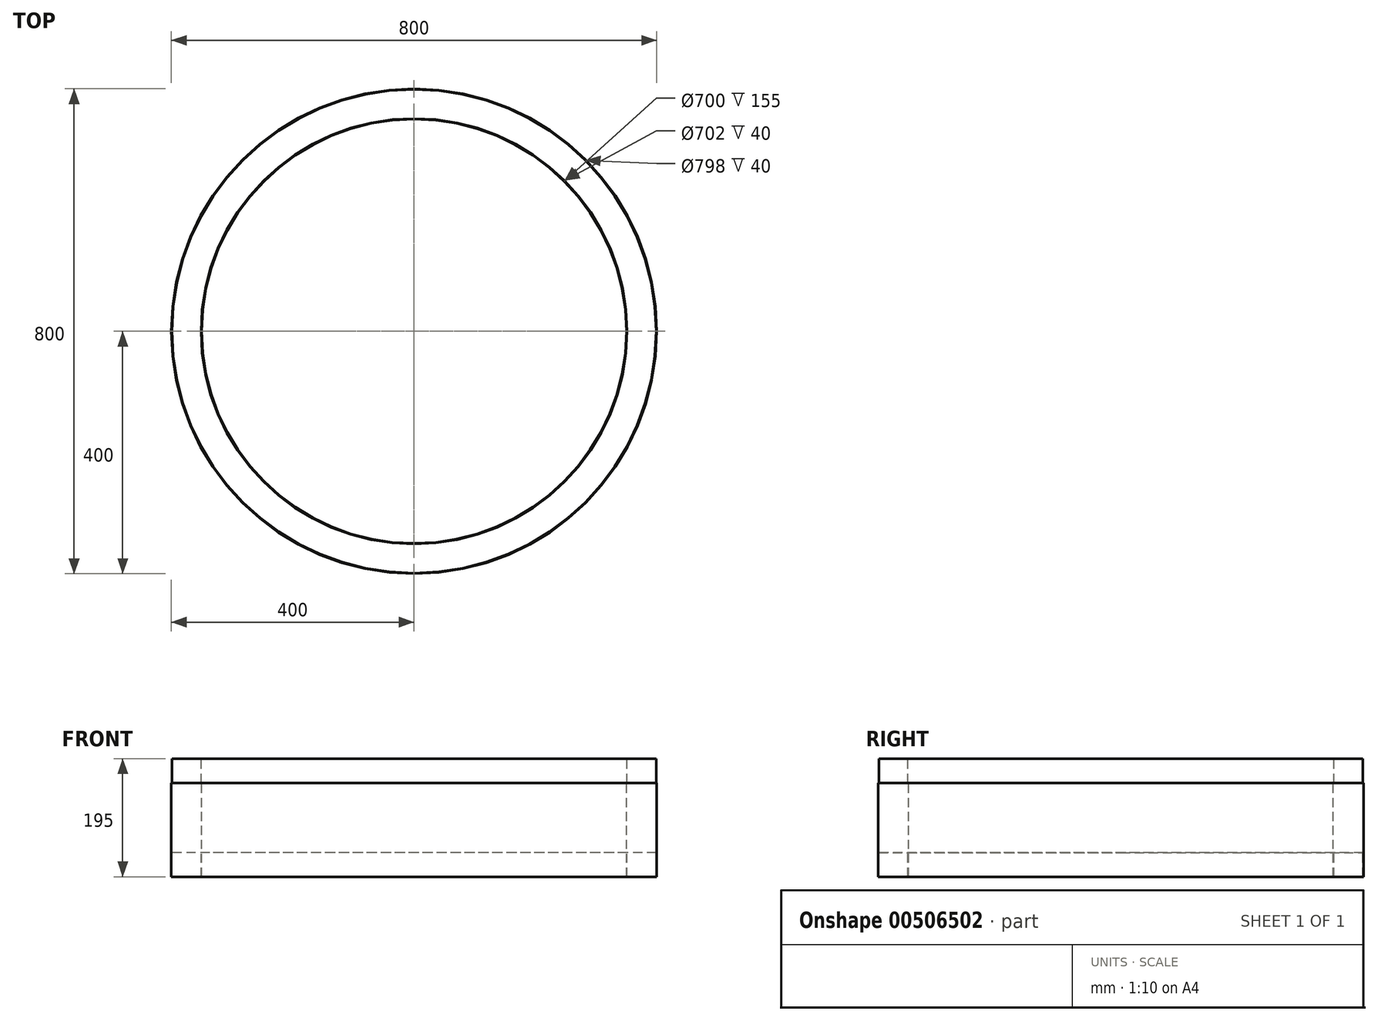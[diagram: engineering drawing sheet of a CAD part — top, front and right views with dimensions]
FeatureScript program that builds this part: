
annotation { "Feature Type Name" : "Feature", "Feature Type Description" : "" }
export const myFeature = defineFeature(function(context is Context, id is Id, definition is map)
    precondition{}
    {
        {
            var Q0;
            Q0=qCreatedBy(makeId("Front.planeOp"),FACE);
            var sketch = newSketch(context, id + "F0", { "sketchPlane" : qUnion([Q0])});
            skLineSegment(sketch, "E0", {"start": v(0, 74.87) * mm, "end": v(0, -73.71) * mm, "construction": true});
            skLineSegment(sketch, "E1", {"start": v(0, 374.84) * mm, "end": v(0, -528.94) * mm, "construction": true});
            skLineSegment(sketch, "E2", {"start": v(-350, -489.75) * mm, "end": v(-350, -334.75) * mm});
            skLineSegment(sketch, "E3", {"start": v(-350, -334.75) * mm, "end": v(-351, -334.75) * mm});
            skLineSegment(sketch, "E4", {"start": v(-351, -334.75) * mm, "end": v(-351, -294.75) * mm});
            skLineSegment(sketch, "E5", {"start": v(-351, -294.75) * mm, "end": v(-399, -294.75) * mm});
            skLineSegment(sketch, "E6", {"start": v(-399, -294.75) * mm, "end": v(-399, -334.75) * mm});
            skLineSegment(sketch, "E7", {"start": v(-399, -334.75) * mm, "end": v(-400, -334.75) * mm});
            skLineSegment(sketch, "E8", {"start": v(-400, -334.75) * mm, "end": v(-400, -489.75) * mm});
            skLineSegment(sketch, "E9", {"start": v(-400, -489.75) * mm, "end": v(-399, -489.75) * mm});
            skLineSegment(sketch, "E10", {"start": v(-399, -489.75) * mm, "end": v(-399, -449.75) * mm});
            skLineSegment(sketch, "E11", {"start": v(-399, -449.75) * mm, "end": v(-351, -449.75) * mm});
            skLineSegment(sketch, "E12", {"start": v(-351, -449.75) * mm, "end": v(-351, -489.75) * mm});
            skLineSegment(sketch, "E13", {"start": v(-351, -489.75) * mm, "end": v(-350, -489.75) * mm});
            skSolve(sketch);
        }
        {
            var Q0;
            Q0=qSketchRegion(id+"F0",true);
            var Q1;
            Q1=sQuery(id+"F0.wireOp",EDGE,"E1");
            revolve(context, id + "F1", {"entities" : qUnion([Q0]), "axis" : qUnion([Q1]), "revolveType" : RevolveType.FULL});
        }
    });
